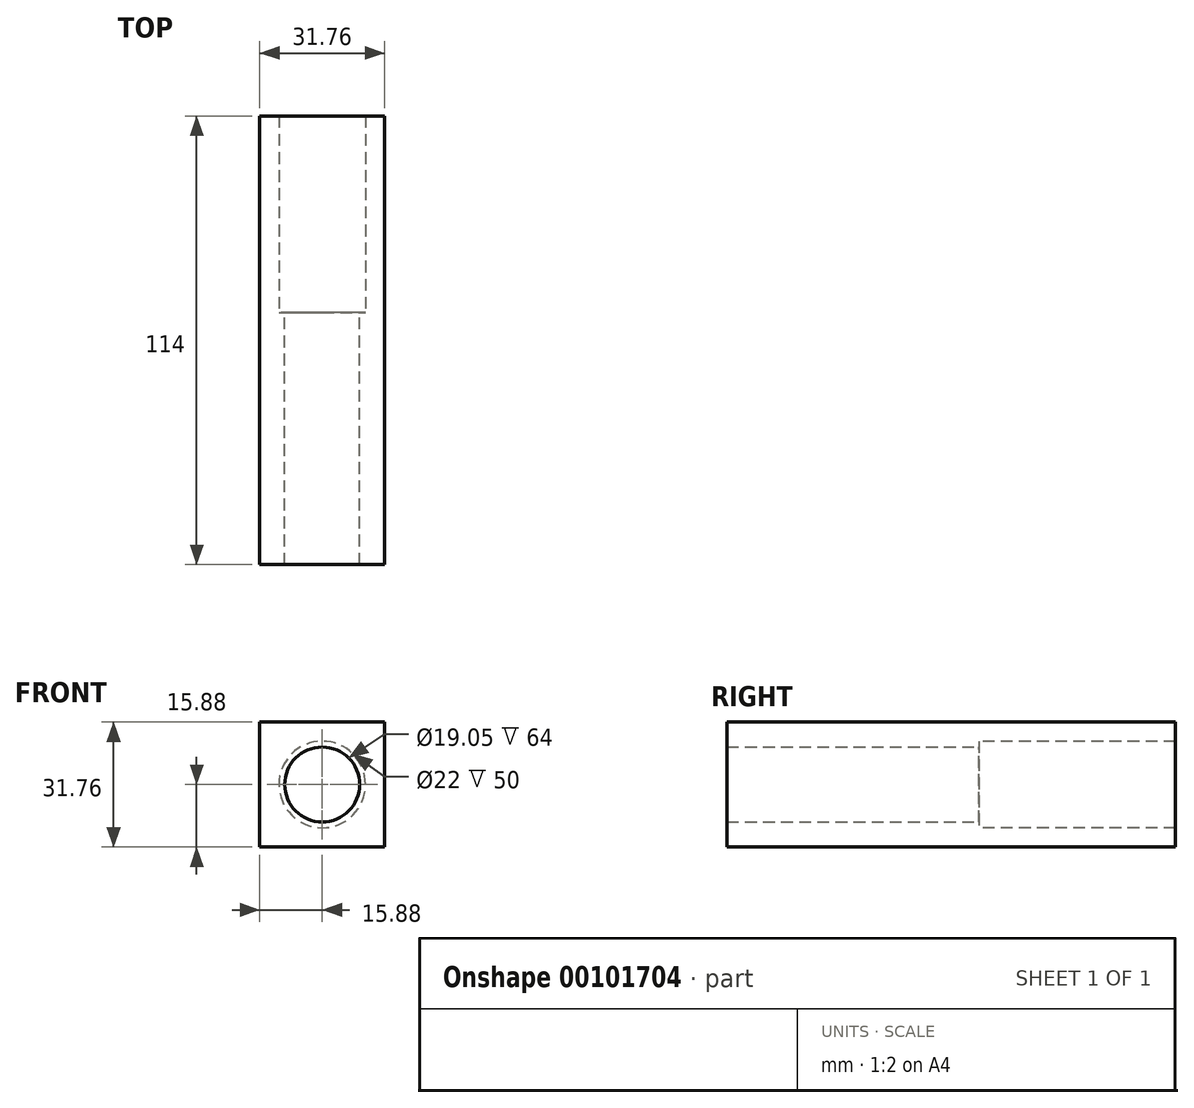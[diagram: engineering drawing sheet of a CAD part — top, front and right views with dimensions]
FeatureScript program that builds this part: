
annotation { "Feature Type Name" : "Feature", "Feature Type Description" : "" }
export const myFeature = defineFeature(function(context is Context, id is Id, definition is map)
    precondition{}
    {
        {
            var Q0;
            Q0=qCreatedBy(makeId("Front.planeOp"),FACE);
            var sketch = newSketch(context, id + "F0", { "sketchPlane" : qUnion([Q0])});
            skLineSegment(sketch, "E0.bottom", {"start": v(-15.88, 15.88) * mm, "end": v(15.88, 15.88) * mm});
            skLineSegment(sketch, "E0.top", {"start": v(-15.88, -15.88) * mm, "end": v(15.88, -15.88) * mm});
            skLineSegment(sketch, "E0.left", {"start": v(-15.88, 15.88) * mm, "end": v(-15.88, -15.88) * mm});
            skLineSegment(sketch, "E0.right", {"start": v(15.88, 15.88) * mm, "end": v(15.88, -15.88) * mm});
            skPoint(sketch, "E0.middle", {"position": v(0, 0) * mm});
            skCircle(sketch, "E1", {"center": v(0, 0) * mm, "radius": 9.53 * mm});
            skSolve(sketch);
        }
        {
            var Q0;
            Q0 = qSketchRegion(id + "F0", true);
            extrude(context, id + "F1", {"entities" : qUnion([Q0]), "depth" : 64 * mm});
        }
        {
            var Q0;
            Q0=makeQuery(id+"F1.opExtrude","CAP_FACE",FACE,{"disambiguationData":[OSD([sQuery(id+"F0.wireOp",EDGE,"E0.bottom"),sQuery(id+"F0.wireOp",EDGE,"E0.top"),sQuery(id+"F0.wireOp",EDGE,"E0.left"),sQuery(id+"F0.wireOp",EDGE,"E0.right"),sQuery(id+"F0.wireOp",EDGE,"E1")])],"isStart":true});
            var sketch = newSketch(context, id + "F2", { "sketchPlane" : qUnion([Q0])});
            skCircle(sketch, "E2", {"center": v(0, 0) * mm, "radius": 11 * mm});
            skLineSegment(sketch, "E3.bottom", {"start": v(15.88, 15.88) * mm, "end": v(-15.88, 15.88) * mm});
            skLineSegment(sketch, "E3.top", {"start": v(15.88, -15.88) * mm, "end": v(-15.88, -15.88) * mm});
            skLineSegment(sketch, "E3.left", {"start": v(15.88, 15.88) * mm, "end": v(15.88, -15.88) * mm});
            skLineSegment(sketch, "E3.right", {"start": v(-15.88, 15.88) * mm, "end": v(-15.88, -15.88) * mm});
            skSolve(sketch);
        }
        {
            var Q0;
            Q0 = qSketchRegion(id + "F2", true);
            extrude(context, id + "F3", {"entities" : qUnion([Q0]), "operationType" : NewBodyOperationType.ADD, "depth" : 50 * mm});
        }
    });
